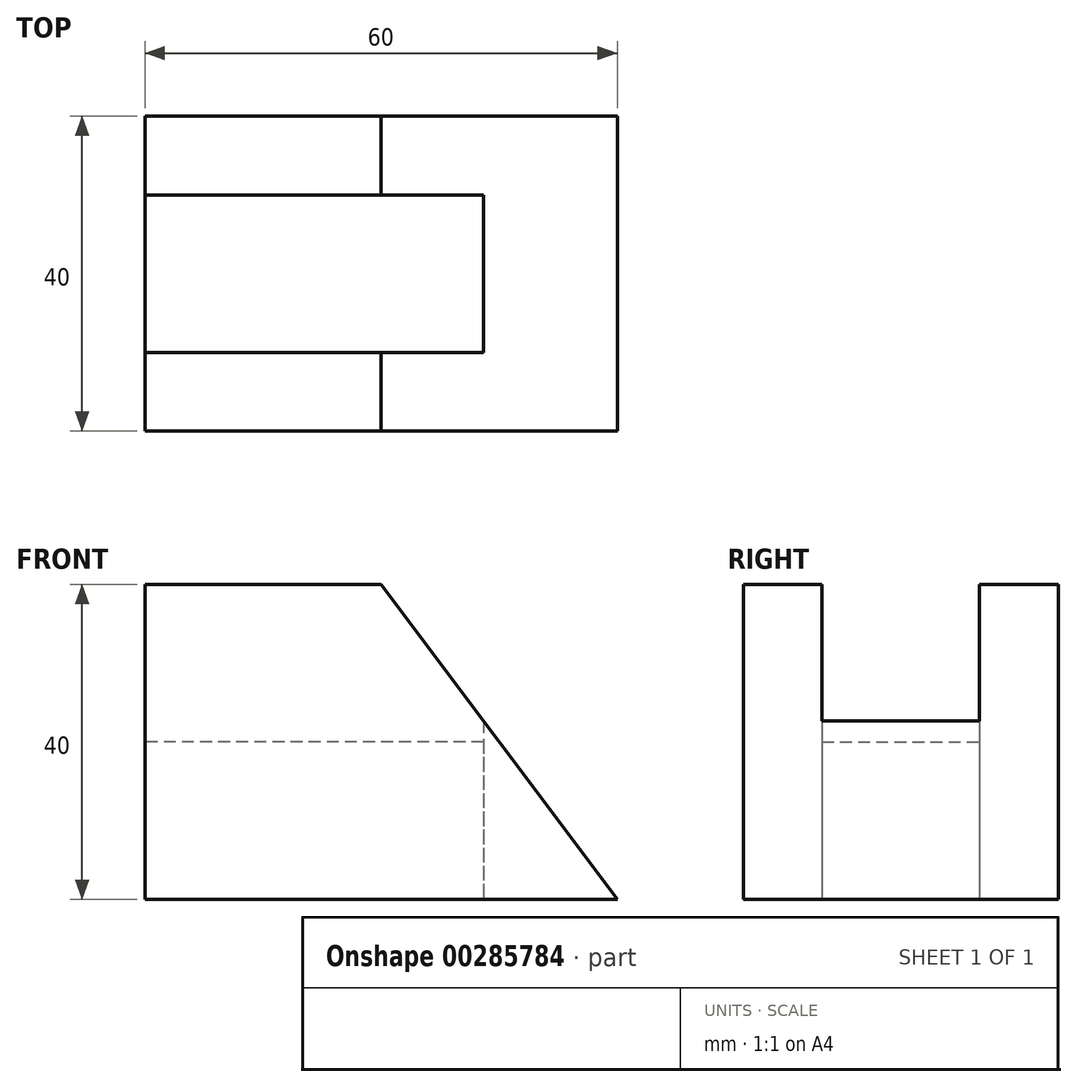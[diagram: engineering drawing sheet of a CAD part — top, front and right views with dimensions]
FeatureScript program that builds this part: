
annotation { "Feature Type Name" : "Feature", "Feature Type Description" : "" }
export const myFeature = defineFeature(function(context is Context, id is Id, definition is map)
    precondition{}
    {
        {
            var Q0;
            Q0=qCreatedBy(makeId("Top.planeOp"),FACE);
            var sketch = newSketch(context, id + "F0", { "sketchPlane" : qUnion([Q0])});
            skLineSegment(sketch, "E0.bottom", {"start": v(0, 0) * mm, "end": v(60, 0) * mm});
            skLineSegment(sketch, "E0.top", {"start": v(0, 40) * mm, "end": v(60, 40) * mm});
            skLineSegment(sketch, "E0.left", {"start": v(0, 0) * mm, "end": v(0, 40) * mm});
            skLineSegment(sketch, "E0.right", {"start": v(60, 0) * mm, "end": v(60, 40) * mm});
            skLineSegment(sketch, "E1", {"start": v(30, 40) * mm, "end": v(30, 30) * mm});
            skPoint(sketch, "E1.startSnap0", {"position": v(30, 40) * mm});
            skLineSegment(sketch, "E2", {"start": v(30, 0) * mm, "end": v(30, 10) * mm});
            skLineSegment(sketch, "E3", {"start": v(30, 10) * mm, "end": v(0, 10) * mm});
            skLineSegment(sketch, "E4", {"start": v(30, 30) * mm, "end": v(0, 30) * mm});
            skLineSegment(sketch, "E5", {"start": v(30, 30) * mm, "end": v(43, 30) * mm});
            skLineSegment(sketch, "E6", {"start": v(43, 30) * mm, "end": v(43, 10) * mm});
            skLineSegment(sketch, "E7", {"start": v(43, 10) * mm, "end": v(30, 10) * mm});
            skSolve(sketch);
        }
        {
            var Q0;
            {var subQ3=sQuery(id+"F0.wireOp",EDGE,"E2");Q0=makeQuery(id+"F0.imprint","IMPRINT",FACE,{"disambiguationData":[TD([[makeQuery(id+"F0.imprint","IMPRINT",EDGE,{"derivedFrom":subQ3}),1.0]])]});}
            var Q1;
            {var subQ3=sQuery(id+"F0.wireOp",EDGE,"E1");Q1=makeQuery(id+"F0.imprint","IMPRINT",FACE,{"disambiguationData":[TD([[makeQuery(id+"F0.imprint","IMPRINT",EDGE,{"derivedFrom":subQ3}),-1.0]])]});}
            var Q2;
            {var subQ0=sQuery(id+"F0.wireOp",EDGE,"E0.right");Q2=makeQuery(id+"F0.imprint","IMPRINT",FACE,{"disambiguationData":[TD([[makeQuery(id+"F0.imprint","IMPRINT",EDGE,{"derivedFrom":subQ0}),1.0]])]});}
            extrude(context, id + "F1", {"entities" : qUnion([Q0, Q1, Q2]), "depth" : 40 * mm});
        }
        {
            var Q0;
            {var subQ1=sQuery(id+"F0.wireOp",EDGE,"E3");Q0=makeQuery(id+"F0.imprint","IMPRINT",FACE,{"disambiguationData":[TD([[makeQuery(id+"F0.imprint","IMPRINT",EDGE,{"derivedFrom":subQ1}),-1.0]])]});}
            extrude(context, id + "F2", {"entities" : qUnion([Q0]), "depth" : 20 * mm});
        }
        {
            var Q0;
            Q0=makeQuery(id+"F1.opExtrude","SWEPT_FACE",FACE,{"disambiguationData":[OSD([sQuery(id+"F0.wireOp",EDGE,"E0.bottom")])]});
            var sketch = newSketch(context, id + "F3", { "sketchPlane" : qUnion([Q0])});
            skLineSegment(sketch, "E8", {"start": v(30, 40) * mm, "end": v(60, 0) * mm});
            skLineSegment(sketch, "E9", {"start": v(60, 0) * mm, "end": v(60, 40) * mm});
            skLineSegment(sketch, "E10", {"start": v(60, 40) * mm, "end": v(30, 40) * mm});
            skSolve(sketch);
        }
        {
            var Q0;
            Q0=makeQuery(id+"F3.imprint","IMPRINT",FACE,{"disambiguationData":[TD([[makeQuery(id+"F3.imprint","IMPRINT",EDGE,{"derivedFrom":sQuery(id+"F3.wireOp",EDGE,"E8")}),1.0]])]});
            extrude(context, id + "F4", {"entities" : qUnion([Q0]), "operationType" : NewBodyOperationType.REMOVE, "oppositeDirection" : true, "depth" : 40 * mm});
        }
    });
